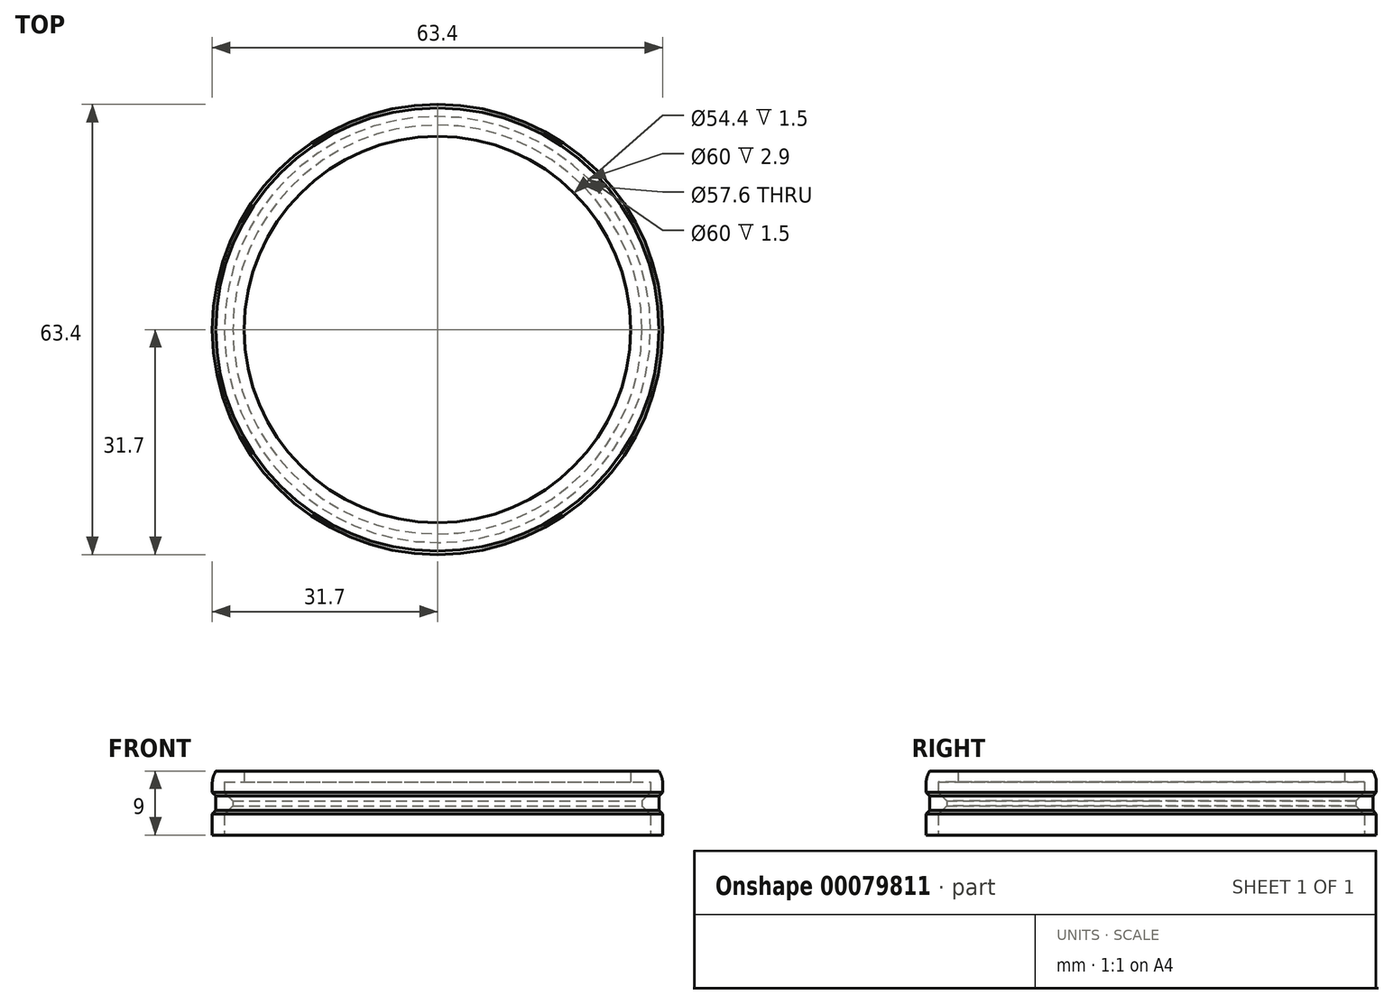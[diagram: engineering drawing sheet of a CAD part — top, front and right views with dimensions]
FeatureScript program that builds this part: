
annotation { "Feature Type Name" : "Feature", "Feature Type Description" : "" }
export const myFeature = defineFeature(function(context is Context, id is Id, definition is map)
    precondition{}
    {
        {
            var Q0;
            Q0=qCreatedBy(makeId("Front.planeOp"),FACE);
            var sketch = newSketch(context, id + "F0", { "sketchPlane" : qUnion([Q0])});
            skLineSegment(sketch, "E0", {"start": v(-30, 3) * mm, "end": v(-30, 0.1) * mm});
            skLineSegment(sketch, "E1", {"start": v(-31.2, 5.6) * mm, "end": v(-31.7, 6.1) * mm});
            skLineSegment(sketch, "E2", {"start": v(-31.7, 6.1) * mm, "end": v(-31.7, 8.23) * mm});
            skLineSegment(sketch, "E3", {"start": v(-31.7, 8.23) * mm, "end": v(-31.2, 9.1) * mm});
            skLineSegment(sketch, "E4", {"start": v(-30, 6.1) * mm, "end": v(-30, 7.6) * mm});
            skLineSegment(sketch, "E5", {"start": v(-30, 7.6) * mm, "end": v(-27.2, 7.6) * mm});
            skLineSegment(sketch, "E6", {"start": v(-27.2, 7.6) * mm, "end": v(-27.2, 9.1) * mm});
            skLineSegment(sketch, "E7", {"start": v(-31.2, 9.1) * mm, "end": v(-27.2, 9.1) * mm});
            skLineSegment(sketch, "E8", {"start": v(0, 0) * mm, "end": v(0, 17.76) * mm});
            skLineSegment(sketch, "E9", {"start": v(-28.8, 4.9) * mm, "end": v(-30, 6.1) * mm});
            skLineSegment(sketch, "E10", {"start": v(-28.8, 4.9) * mm, "end": v(-28.8, 4.2) * mm});
            skLineSegment(sketch, "E11", {"start": v(-28.8, 4.2) * mm, "end": v(-30, 3) * mm});
            skLineSegment(sketch, "E12", {"start": v(-31.2, 5.6) * mm, "end": v(-31.2, 3.6) * mm});
            skLineSegment(sketch, "E13", {"start": v(-31.2, 3.6) * mm, "end": v(-31.7, 3.1) * mm});
            skLineSegment(sketch, "E14", {"start": v(-31.7, 3.1) * mm, "end": v(-31.7, 0.1) * mm});
            skLineSegment(sketch, "E15", {"start": v(-31.7, 0.1) * mm, "end": v(-30, 0.1) * mm});
            skSolve(sketch);
        }
        {
            var Q0;
            Q0=makeQuery(id+"F0.imprint","IMPRINT",FACE,{"disambiguationData":[TD([[makeQuery(id+"F0.imprint","IMPRINT",EDGE,{"derivedFrom":sQuery(id+"F0.wireOp",EDGE,"cdW0xtgF-uYVp-RtY3-ap5X-TR9GfRdG24Iu")}),-1.0]])]});
            var Q1;
            Q1=makeQuery(id+"F0.imprint","IMPRINT",FACE,{"disambiguationData":[TD([[makeQuery(id+"F0.imprint","IMPRINT",EDGE,{"derivedFrom":sQuery(id+"F0.wireOp",EDGE,"bWv10M2c-J1HN-FUTH-utHm-dLCi9WMXUi7r")}),-1.0]])]});
            var Q2;
            Q2=makeQuery(id+"F0.imprint","IMPRINT",FACE,{"disambiguationData":[TD([[makeQuery(id+"F0.imprint","IMPRINT",EDGE,{"derivedFrom":sQuery(id+"F0.wireOp",EDGE,"E0")}),-1.0]])]});
            var Q3;
            Q3=sQuery(id+"F0.wireOp",EDGE,"E8");
            revolve(context, id + "F1", {"entities" : qUnion([Q0, Q1, Q2]), "axis" : qUnion([Q3]), "revolveType" : RevolveType.FULL});
        }
        {
            var Q0;
            Q0=makeQuery(id+"F1.opRevolve","SWEPT_EDGE",EDGE,{"disambiguationData":[OSD([sQuery(id+"F0.wireOp",EDGE,"E2"),sQuery(id+"F0.wireOp",EDGE,"E3")])]});
            fillet(context, id + "F2", {"entities" : qUnion([Q0]), "radius" : 3 * mm, "tangentPropagation" : true, "allowEdgeOverflow" : false});
        }
    });
